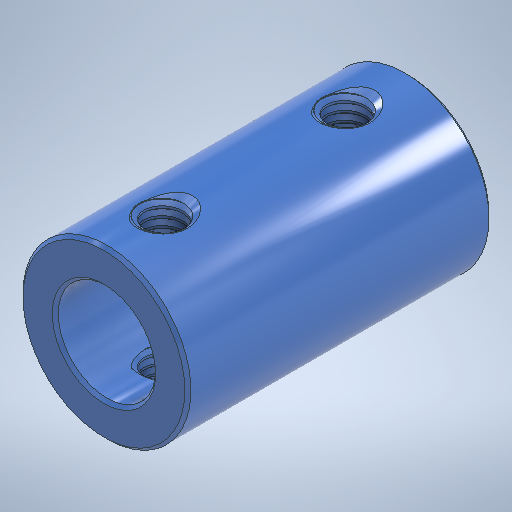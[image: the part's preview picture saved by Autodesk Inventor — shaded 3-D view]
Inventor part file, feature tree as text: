
AUTODESK INVENTOR PART (.ipt)
format: ipt  version: 2025.2 (Build 292293000, 293)  size: 945,152 bytes
history: native  units: in
note: dims shown in document units (in); Inventor stores cm internally (conversion verified against a paired STEP export)
features: thread x1
ambient origin geometry x8: Origin, YZ Plane, XZ Plane, XY Plane, X Axis, Y Axis, Z Axis, Center Point
bodies: Solid1 (feature_tree)
feature tree (1):
  thread  "Thread2"  [1 undecoded]
note: 1 required parameter value undecoded (feature->parameter linkage not recoverable at this tier; creation-order binding heuristic only, values carry confidence <= 0.55)
